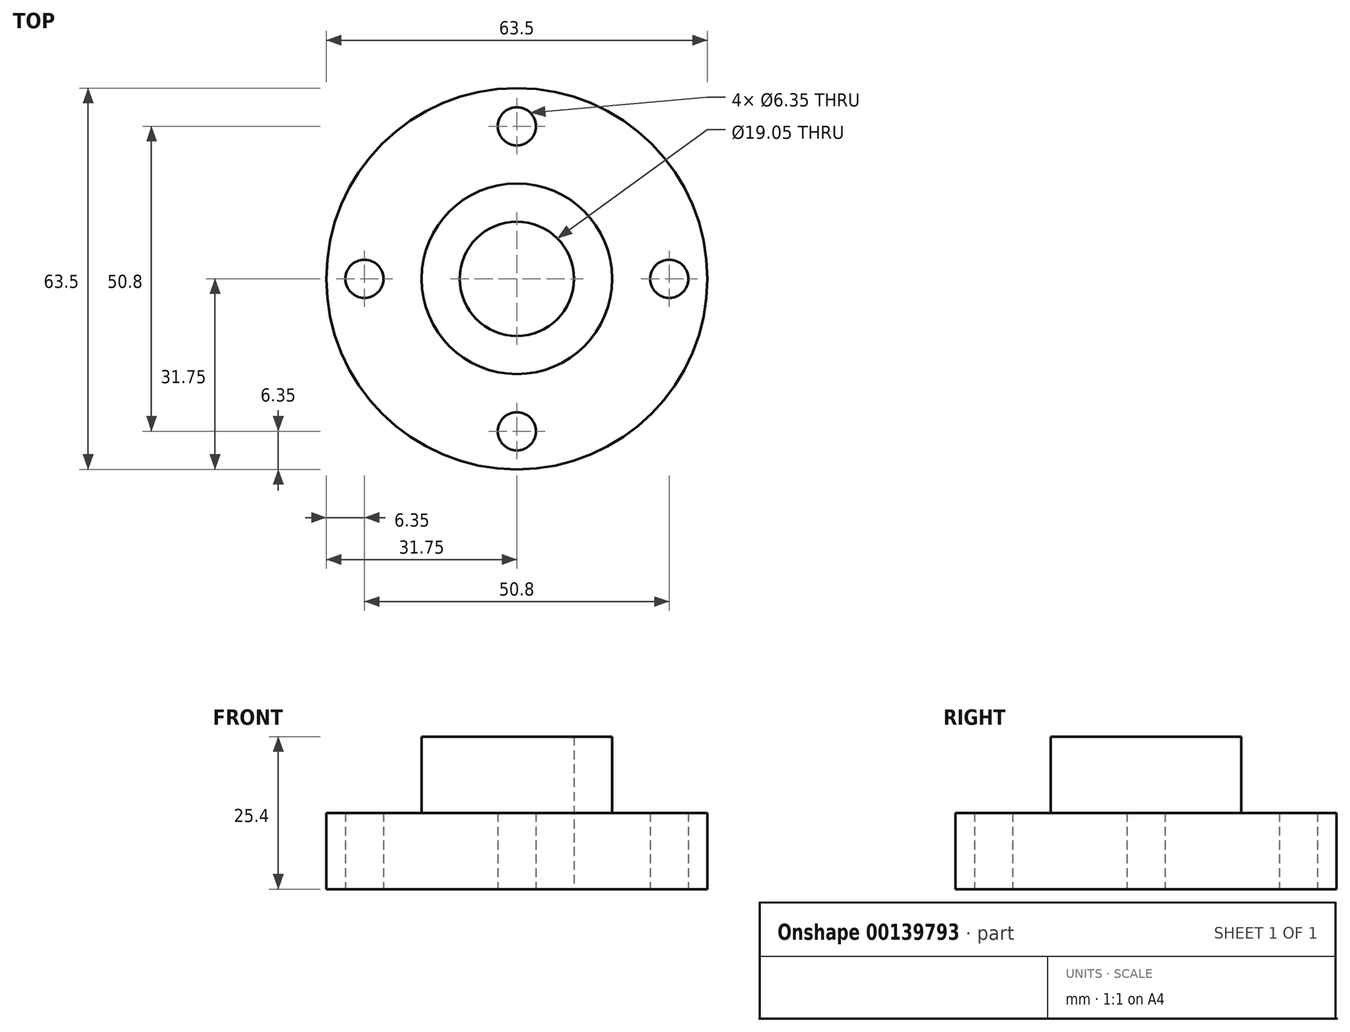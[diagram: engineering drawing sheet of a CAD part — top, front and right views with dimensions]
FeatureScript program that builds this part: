
annotation { "Feature Type Name" : "Feature", "Feature Type Description" : "" }
export const myFeature = defineFeature(function(context is Context, id is Id, definition is map)
    precondition{}
    {
        {
            var Q0;
            Q0=qCreatedBy(makeId("Top.planeOp"),FACE);
            var sketch = newSketch(context, id + "F0", { "sketchPlane" : qUnion([Q0])});
            skCircle(sketch, "E0", {"center": v(0, 0) * mm, "radius": 31.75 * mm});
            skCircle(sketch, "E1", {"center": v(0, 0) * mm, "radius": 15.88 * mm});
            skCircle(sketch, "E2", {"center": v(0, 0) * mm, "radius": 9.53 * mm});
            skCircle(sketch, "E3", {"center": v(0, 25.4) * mm, "radius": 3.18 * mm});
            skCircle(sketch, "E4.1.0", {"center": v(-25.4, 0) * mm, "radius": 3.18 * mm});
            skCircle(sketch, "E4.2.0", {"center": v(0, -25.4) * mm, "radius": 3.18 * mm});
            skCircle(sketch, "E4.3.0", {"center": v(25.4, 0) * mm, "radius": 3.18 * mm});
            skSolve(sketch);
        }
        {
            var Q0;
            Q0=makeQuery(id+"F0.imprint","IMPRINT",FACE,{"disambiguationData":[TD([[makeQuery(id+"F0.imprint","IMPRINT",EDGE,{"derivedFrom":sQuery(id+"F0.wireOp",EDGE,"E1")}),1.0]])]});
            extrude(context, id + "F1", {"entities" : qUnion([Q0]), "depth" : 25.4 * mm});
        }
        {
            var Q0;
            Q0=makeQuery(id+"F0.imprint","IMPRINT",FACE,{"disambiguationData":[TD([[makeQuery(id+"F0.imprint","IMPRINT",EDGE,{"derivedFrom":sQuery(id+"F0.wireOp",EDGE,"E0")}),1.0]])]});
            extrude(context, id + "F2", {"entities" : qUnion([Q0]), "operationType" : NewBodyOperationType.ADD, "depth" : 12.7 * mm});
        }
    });
